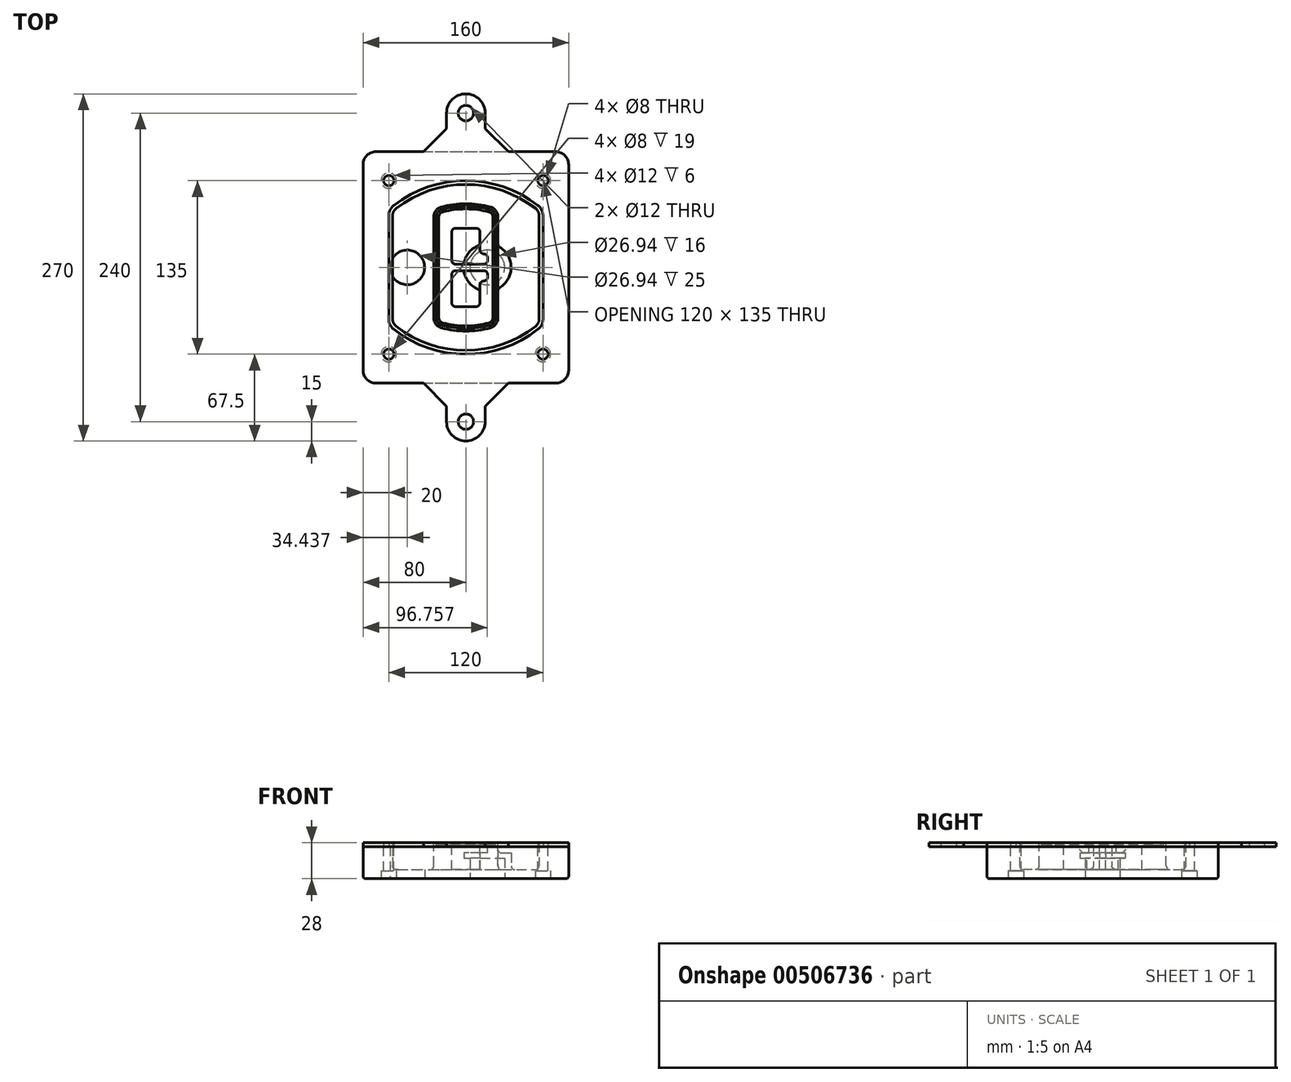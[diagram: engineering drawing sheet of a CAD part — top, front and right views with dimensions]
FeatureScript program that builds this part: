
annotation { "Feature Type Name" : "Feature", "Feature Type Description" : "" }
export const myFeature = defineFeature(function(context is Context, id is Id, definition is map)
    precondition{}
    {
        {
            var Q0;
            Q0=qCreatedBy(makeId("Top.planeOp"),FACE);
            var sketch = newSketch(context, id + "F0", { "sketchPlane" : qUnion([Q0])});
            skPoint(sketch, "E0.rect.middle", {"position": v(0, 0) * mm});
            skLineSegment(sketch, "E1.bottom", {"start": v(-70, -90) * mm, "end": v(70, -90) * mm});
            skLineSegment(sketch, "E1.top", {"start": v(-70, 90) * mm, "end": v(70, 90) * mm});
            skLineSegment(sketch, "E1.left", {"start": v(-80, -80) * mm, "end": v(-80, 80) * mm});
            skLineSegment(sketch, "E1.right", {"start": v(80, -80) * mm, "end": v(80, 80) * mm});
            skLineSegment(sketch, "E2", {"start": v(-80, 90) * mm, "end": v(80, -90) * mm, "construction": true});
            skLineSegment(sketch, "E3", {"start": v(80, 90) * mm, "end": v(-80, -90) * mm, "construction": true});
            skCircle(sketch, "E4", {"center": v(-60, 67.5) * mm, "radius": 4 * mm});
            skCircle(sketch, "E5", {"center": v(60, 67.5) * mm, "radius": 4 * mm});
            skCircle(sketch, "E6", {"center": v(60, -67.5) * mm, "radius": 4 * mm});
            skCircle(sketch, "E7", {"center": v(-60, -67.5) * mm, "radius": 4 * mm});
            skLineSegment(sketch, "E8", {"start": v(-60, 67.5) * mm, "end": v(60, 67.5) * mm, "construction": true});
            skLineSegment(sketch, "E9", {"start": v(60, 67.5) * mm, "end": v(60, -67.5) * mm, "construction": true});
            skLineSegment(sketch, "E10", {"start": v(60, -67.5) * mm, "end": v(-60, -67.5) * mm, "construction": true});
            skLineSegment(sketch, "E11", {"start": v(-60, -67.5) * mm, "end": v(-60, 67.5) * mm, "construction": true});
            skLineSegment(sketch, "E12", {"start": v(-60, 40.3) * mm, "end": v(-60, -40.3) * mm});
            skLineSegment(sketch, "E13", {"start": v(60, 40.3) * mm, "end": v(60, -40.3) * mm});
            skArc(sketch, "E14", {"start": v(56.15, 48.18) * mm, "mid": v(0, 67.5) * mm, "end": v(-56.15, 48.18) * mm});
            skArc(sketch, "E15", {"start": v(-56.15, -48.18) * mm, "mid": v(0, -67.5) * mm, "end": v(56.15, -48.18) * mm});
            skLineSegment(sketch, "E16", {"start": v(-60, 0) * mm, "end": v(60, 0) * mm, "construction": true});
            skPoint(sketch, "E17.visualSharp", {"position": v(-60, -45) * mm});
            skArc(sketch, "E17.filletArc", {"start": v(-60, -40.3) * mm, "mid": v(-58.99, -44.68) * mm, "end": v(-56.15, -48.18) * mm});
            skPoint(sketch, "E18.visualSharp", {"position": v(-60, 45) * mm});
            skArc(sketch, "E18.filletArc", {"start": v(-56.15, 48.18) * mm, "mid": v(-58.99, 44.68) * mm, "end": v(-60, 40.3) * mm});
            skPoint(sketch, "E19.visualSharp", {"position": v(60, 45) * mm});
            skArc(sketch, "E19.filletArc", {"start": v(60, 40.3) * mm, "mid": v(58.99, 44.68) * mm, "end": v(56.15, 48.18) * mm});
            skPoint(sketch, "E20.visualSharp", {"position": v(60, -45) * mm});
            skArc(sketch, "E20.filletArc", {"start": v(56.15, -48.18) * mm, "mid": v(58.99, -44.68) * mm, "end": v(60, -40.3) * mm});
            skPoint(sketch, "E21.visualSharp", {"position": v(-80, 90) * mm});
            skArc(sketch, "E21.filletArc", {"start": v(-70, 90) * mm, "mid": v(-77.07, 87.07) * mm, "end": v(-80, 80) * mm});
            skPoint(sketch, "E22.visualSharp", {"position": v(80, 90) * mm});
            skArc(sketch, "E22.filletArc", {"start": v(80, 80) * mm, "mid": v(77.07, 87.07) * mm, "end": v(70, 90) * mm});
            skPoint(sketch, "E23.visualSharp", {"position": v(80, -90) * mm});
            skArc(sketch, "E23.filletArc", {"start": v(70, -90) * mm, "mid": v(77.07, -87.07) * mm, "end": v(80, -80) * mm});
            skPoint(sketch, "E24.visualSharp", {"position": v(-80, -90) * mm});
            skArc(sketch, "E24.filletArc", {"start": v(-80, -80) * mm, "mid": v(-77.07, -87.07) * mm, "end": v(-70, -90) * mm});
            skArc(sketch, "E25.0", {"start": v(57, 40.3) * mm, "mid": v(56.3, 43.36) * mm, "end": v(54.3, 45.81) * mm});
            skLineSegment(sketch, "E25.1", {"start": v(57, 40.3) * mm, "end": v(57, -40.3) * mm});
            skArc(sketch, "E25.2", {"start": v(54.3, -45.81) * mm, "mid": v(56.3, -43.36) * mm, "end": v(57, -40.3) * mm});
            skArc(sketch, "E25.3", {"start": v(-54.3, -45.81) * mm, "mid": v(0, -64.5) * mm, "end": v(54.3, -45.81) * mm});
            skArc(sketch, "E25.4", {"start": v(-57, -40.3) * mm, "mid": v(-56.3, -43.36) * mm, "end": v(-54.3, -45.81) * mm});
            skArc(sketch, "E25.5", {"start": v(54.3, 45.81) * mm, "mid": v(0, 64.5) * mm, "end": v(-54.3, 45.81) * mm});
            skLineSegment(sketch, "E25.6", {"start": v(-57, 40.3) * mm, "end": v(-57, -40.3) * mm});
            skArc(sketch, "E25.7", {"start": v(-54.3, 45.81) * mm, "mid": v(-56.3, 43.36) * mm, "end": v(-57, 40.3) * mm});
            skArc(sketch, "E26.0", {"start": v(-58.62, 51.33) * mm, "mid": v(-62.58, 46.43) * mm, "end": v(-64, 40.3) * mm});
            skArc(sketch, "E26.1", {"start": v(58.62, 51.33) * mm, "mid": v(0, 71.5) * mm, "end": v(-58.62, 51.33) * mm});
            skArc(sketch, "E26.2", {"start": v(64, 40.3) * mm, "mid": v(62.58, 46.43) * mm, "end": v(58.62, 51.33) * mm});
            skLineSegment(sketch, "E26.3", {"start": v(64, 40.3) * mm, "end": v(64, -40.3) * mm});
            skArc(sketch, "E26.4", {"start": v(58.62, -51.33) * mm, "mid": v(62.58, -46.43) * mm, "end": v(64, -40.3) * mm});
            skLineSegment(sketch, "E26.5", {"start": v(-64, 40.3) * mm, "end": v(-64, -40.3) * mm});
            skArc(sketch, "E26.6", {"start": v(-58.62, -51.33) * mm, "mid": v(0, -71.5) * mm, "end": v(58.62, -51.33) * mm});
            skArc(sketch, "E26.7", {"start": v(-64, -40.3) * mm, "mid": v(-62.58, -46.43) * mm, "end": v(-58.62, -51.33) * mm});
            skSolve(sketch);
        }
        {
            var Q0;
            Q0=makeQuery(id+"F0.imprint","IMPRINT",FACE,{"disambiguationData":[TD([[makeQuery(id+"F0.imprint","IMPRINT",EDGE,{"derivedFrom":sQuery(id+"F0.wireOp",EDGE,"E1.bottom")}),1.0]])]});
            var Q1;
            Q1=makeQuery(id+"F0.imprint","IMPRINT",FACE,{"disambiguationData":[TD([[makeQuery(id+"F0.imprint","IMPRINT",EDGE,{"derivedFrom":sQuery(id+"F0.wireOp",EDGE,"E12")}),1.0]])]});
            var Q2;
            Q2=makeQuery(id+"F0.imprint","IMPRINT",FACE,{"disambiguationData":[TD([[makeQuery(id+"F0.imprint","IMPRINT",EDGE,{"derivedFrom":sQuery(id+"F0.wireOp",EDGE,"E25.0")}),1.0]])]});
            var Q3;
            Q3=makeQuery(id+"F0.imprint","IMPRINT",FACE,{"disambiguationData":[TD([[makeQuery(id+"F0.imprint","IMPRINT",EDGE,{"derivedFrom":sQuery(id+"F0.wireOp",EDGE,"E12")}),-1.0]])]});
            extrude(context, id + "F1", {"entities" : qUnion([Q0, Q1, Q2, Q3]), "oppositeDirection" : true, "depth" : 25 * mm});
        }
        {
            var Q0;
            Q0=makeQuery(id+"F0.imprint","IMPRINT",FACE,{"disambiguationData":[TD([[makeQuery(id+"F0.imprint","IMPRINT",EDGE,{"derivedFrom":sQuery(id+"F0.wireOp",EDGE,"E12")}),1.0]])]});
            extrude(context, id + "F2", {"entities" : qUnion([Q0]), "operationType" : NewBodyOperationType.ADD, "depth" : 3 * mm});
        }
        {
            var Q0;
            Q0=makeQuery(id+"F0.imprint","IMPRINT",FACE,{"disambiguationData":[TD([[makeQuery(id+"F0.imprint","IMPRINT",EDGE,{"derivedFrom":sQuery(id+"F0.wireOp",EDGE,"E25.0")}),1.0]])]});
            extrude(context, id + "F3", {"entities" : qUnion([Q0]), "operationType" : NewBodyOperationType.REMOVE, "oppositeDirection" : true, "depth" : 18 * mm});
        }
        {
            var Q0;
            Q0=makeQuery(id+"F2.opExtrude","CAP_FACE",FACE,{"disambiguationData":[OSD([sQuery(id+"F0.wireOp",EDGE,"E12"),sQuery(id+"F0.wireOp",EDGE,"E13"),sQuery(id+"F0.wireOp",EDGE,"E14"),sQuery(id+"F0.wireOp",EDGE,"E15"),sQuery(id+"F0.wireOp",EDGE,"E17.filletArc"),sQuery(id+"F0.wireOp",EDGE,"E18.filletArc"),sQuery(id+"F0.wireOp",EDGE,"E19.filletArc"),sQuery(id+"F0.wireOp",EDGE,"E20.filletArc"),sQuery(id+"F0.wireOp",EDGE,"E25.0"),sQuery(id+"F0.wireOp",EDGE,"E25.1"),sQuery(id+"F0.wireOp",EDGE,"E25.2"),sQuery(id+"F0.wireOp",EDGE,"E25.3"),sQuery(id+"F0.wireOp",EDGE,"E25.4"),sQuery(id+"F0.wireOp",EDGE,"E25.5"),sQuery(id+"F0.wireOp",EDGE,"E25.6"),sQuery(id+"F0.wireOp",EDGE,"E25.7")])],"isStart":false});
            var sketch = newSketch(context, id + "F4", { "sketchPlane" : qUnion([Q0])});
            skArc(sketch, "E27.0", {"start": v(-19.08, -46.97) * mm, "mid": v(0, -49.5) * mm, "end": v(19.08, -46.97) * mm});
            skArc(sketch, "E28.0", {"start": v(19.08, 46.97) * mm, "mid": v(0, 49.5) * mm, "end": v(-19.08, 46.97) * mm});
            skLineSegment(sketch, "E29", {"start": v(-25, 39.25) * mm, "end": v(-25, -39.25) * mm});
            skLineSegment(sketch, "E30", {"start": v(25, 39.25) * mm, "end": v(25, -39.25) * mm});
            skLineSegment(sketch, "E31", {"start": v(-25, 45.1) * mm, "end": v(25, 45.1) * mm, "construction": true});
            skLineSegment(sketch, "E32", {"start": v(-25, -45.1) * mm, "end": v(25, -45.1) * mm, "construction": true});
            skPoint(sketch, "E33.visualSharp", {"position": v(-25, 45.1) * mm});
            skArc(sketch, "E33.filletArc", {"start": v(-19.08, 46.97) * mm, "mid": v(-23.35, 44.11) * mm, "end": v(-25, 39.25) * mm});
            skPoint(sketch, "E34.visualSharp", {"position": v(25, 45.1) * mm});
            skArc(sketch, "E34.filletArc", {"start": v(25, 39.25) * mm, "mid": v(23.35, 44.11) * mm, "end": v(19.08, 46.97) * mm});
            skPoint(sketch, "E35.visualSharp", {"position": v(25, -45.1) * mm});
            skArc(sketch, "E35.filletArc", {"start": v(19.08, -46.97) * mm, "mid": v(23.35, -44.11) * mm, "end": v(25, -39.25) * mm});
            skPoint(sketch, "E36.visualSharp", {"position": v(-25, -45.1) * mm});
            skArc(sketch, "E36.filletArc", {"start": v(-25, -39.25) * mm, "mid": v(-23.35, -44.11) * mm, "end": v(-19.08, -46.97) * mm});
            skArc(sketch, "E37.0", {"start": v(54.3, 45.81) * mm, "mid": v(0, 64.5) * mm, "end": v(-54.3, 45.81) * mm});
            skArc(sketch, "E37.1", {"start": v(-54.3, 45.81) * mm, "mid": v(-56.3, 43.36) * mm, "end": v(-57, 40.3) * mm});
            skLineSegment(sketch, "E37.2", {"start": v(-57, 40.3) * mm, "end": v(-57, -40.3) * mm});
            skArc(sketch, "E37.3", {"start": v(-57, -40.3) * mm, "mid": v(-56.3, -43.36) * mm, "end": v(-54.3, -45.81) * mm});
            skArc(sketch, "E37.4", {"start": v(-54.3, -45.81) * mm, "mid": v(0, -64.5) * mm, "end": v(54.3, -45.81) * mm});
            skArc(sketch, "E37.5", {"start": v(54.3, -45.81) * mm, "mid": v(56.3, -43.36) * mm, "end": v(57, -40.3) * mm});
            skLineSegment(sketch, "E37.6", {"start": v(57, 40.3) * mm, "end": v(57, -40.3) * mm});
            skArc(sketch, "E37.7", {"start": v(57, 40.3) * mm, "mid": v(56.3, 43.36) * mm, "end": v(54.3, 45.81) * mm});
            skLineSegment(sketch, "E38.0", {"start": v(23, 39.25) * mm, "end": v(23, -39.25) * mm});
            skArc(sketch, "E38.1", {"start": v(18.56, -45.04) * mm, "mid": v(21.76, -42.9) * mm, "end": v(23, -39.25) * mm});
            skArc(sketch, "E38.2", {"start": v(-18.56, -45.04) * mm, "mid": v(0, -47.5) * mm, "end": v(18.56, -45.04) * mm});
            skArc(sketch, "E38.3", {"start": v(-23, -39.25) * mm, "mid": v(-21.76, -42.9) * mm, "end": v(-18.56, -45.04) * mm});
            skLineSegment(sketch, "E38.4", {"start": v(-23, 39.25) * mm, "end": v(-23, -39.25) * mm});
            skArc(sketch, "E38.5", {"start": v(23, 39.25) * mm, "mid": v(21.76, 42.9) * mm, "end": v(18.56, 45.04) * mm});
            skArc(sketch, "E38.6", {"start": v(-18.56, 45.04) * mm, "mid": v(-21.76, 42.9) * mm, "end": v(-23, 39.25) * mm});
            skArc(sketch, "E38.7", {"start": v(18.56, 45.04) * mm, "mid": v(0, 47.5) * mm, "end": v(-18.56, 45.04) * mm});
            skArc(sketch, "E39.0", {"start": v(21, 39.25) * mm, "mid": v(20.18, 41.68) * mm, "end": v(18.04, 43.1) * mm});
            skLineSegment(sketch, "E39.1", {"start": v(21, 39.25) * mm, "end": v(21, -39.25) * mm});
            skArc(sketch, "E39.2", {"start": v(18.04, -43.1) * mm, "mid": v(20.18, -41.68) * mm, "end": v(21, -39.25) * mm});
            skArc(sketch, "E39.3", {"start": v(-18.04, -43.1) * mm, "mid": v(0, -45.5) * mm, "end": v(18.04, -43.1) * mm});
            skArc(sketch, "E39.4", {"start": v(-21, -39.25) * mm, "mid": v(-20.18, -41.68) * mm, "end": v(-18.04, -43.1) * mm});
            skArc(sketch, "E39.5", {"start": v(18.04, 43.1) * mm, "mid": v(0, 45.5) * mm, "end": v(-18.04, 43.1) * mm});
            skLineSegment(sketch, "E39.6", {"start": v(-21, 39.25) * mm, "end": v(-21, -39.25) * mm});
            skArc(sketch, "E39.7", {"start": v(-18.04, 43.1) * mm, "mid": v(-20.18, 41.68) * mm, "end": v(-21, 39.25) * mm});
            skLineSegment(sketch, "E40", {"start": v(-25, 0) * mm, "end": v(25, 0) * mm, "construction": true});
            skLineSegment(sketch, "E41", {"start": v(-11, 5.5) * mm, "end": v(-11, 27.5) * mm});
            skLineSegment(sketch, "E42", {"start": v(-8, 30.5) * mm, "end": v(8, 30.5) * mm});
            skLineSegment(sketch, "E43", {"start": v(11, 27.5) * mm, "end": v(11, 13.5) * mm});
            skLineSegment(sketch, "E44", {"start": v(14, 10.5) * mm, "end": v(14, 10.5) * mm});
            skLineSegment(sketch, "E45", {"start": v(17, 7.5) * mm, "end": v(17, 5.5) * mm});
            skLineSegment(sketch, "E46", {"start": v(14, 2.5) * mm, "end": v(-8, 2.5) * mm});
            skPoint(sketch, "E47.visualSharp", {"position": v(-11, 30.5) * mm});
            skArc(sketch, "E47.filletArc", {"start": v(-8, 30.5) * mm, "mid": v(-10.12, 29.62) * mm, "end": v(-11, 27.5) * mm});
            skPoint(sketch, "E48.visualSharp", {"position": v(11, 30.5) * mm});
            skArc(sketch, "E48.filletArc", {"start": v(11, 27.5) * mm, "mid": v(10.12, 29.62) * mm, "end": v(8, 30.5) * mm});
            skPoint(sketch, "E49.visualSharp", {"position": v(11, 10.5) * mm});
            skArc(sketch, "E49.filletArc", {"start": v(11, 13.5) * mm, "mid": v(11.88, 11.38) * mm, "end": v(14, 10.5) * mm});
            skPoint(sketch, "E50.visualSharp", {"position": v(17, 10.5) * mm});
            skArc(sketch, "E50.filletArc", {"start": v(17, 7.5) * mm, "mid": v(16.12, 9.62) * mm, "end": v(14, 10.5) * mm});
            skPoint(sketch, "E51.visualSharp", {"position": v(17, 2.5) * mm});
            skArc(sketch, "E51.filletArc", {"start": v(14, 2.5) * mm, "mid": v(16.12, 3.38) * mm, "end": v(17, 5.5) * mm});
            skPoint(sketch, "E52.visualSharp", {"position": v(-11, 2.5) * mm});
            skArc(sketch, "E52.filletArc", {"start": v(-11, 5.5) * mm, "mid": v(-10.12, 3.38) * mm, "end": v(-8, 2.5) * mm});
            skLineSegment(sketch, "E53.0.MirrorCS", {"start": v(14, -2.5) * mm, "end": v(-8, -2.5) * mm});
            skArc(sketch, "E54.0.MirrorCS", {"start": v(-11, -5.5) * mm, "mid": v(-10.12, -3.38) * mm, "end": v(-8, -2.5) * mm});
            skLineSegment(sketch, "E55.0.MirrorCS", {"start": v(-11, -5.5) * mm, "end": v(-11, -27.5) * mm});
            skArc(sketch, "E56.0.MirrorCS", {"start": v(-8, -30.5) * mm, "mid": v(-10.12, -29.62) * mm, "end": v(-11, -27.5) * mm});
            skLineSegment(sketch, "E57.0.MirrorCS", {"start": v(-8, -30.5) * mm, "end": v(8, -30.5) * mm});
            skArc(sketch, "E58.0.MirrorCS", {"start": v(11, -27.5) * mm, "mid": v(10.12, -29.62) * mm, "end": v(8, -30.5) * mm});
            skLineSegment(sketch, "E59.0.MirrorCS", {"start": v(11, -27.5) * mm, "end": v(11, -13.5) * mm});
            skArc(sketch, "E60.0.MirrorCS", {"start": v(11, -13.5) * mm, "mid": v(11.88, -11.38) * mm, "end": v(14, -10.5) * mm});
            skArc(sketch, "E61.0.MirrorCS", {"start": v(17, -7.5) * mm, "mid": v(16.12, -9.62) * mm, "end": v(14, -10.5) * mm});
            skLineSegment(sketch, "E62.0.MirrorCS", {"start": v(17, -7.5) * mm, "end": v(17, -5.5) * mm});
            skArc(sketch, "E63.0.MirrorCS", {"start": v(14, -2.5) * mm, "mid": v(16.12, -3.38) * mm, "end": v(17, -5.5) * mm});
            skSolve(sketch);
        }
        {
            var Q0;
            Q0=makeQuery(id+"F4.imprint","IMPRINT",FACE,{"disambiguationData":[TD([[makeQuery(id+"F4.imprint","IMPRINT",EDGE,{"derivedFrom":sQuery(id+"F4.wireOp",EDGE,"E27.0")}),1.0]])]});
            var Q1;
            Q1=makeQuery(id+"F4.imprint","IMPRINT",FACE,{"disambiguationData":[TD([[makeQuery(id+"F4.imprint","IMPRINT",EDGE,{"derivedFrom":sQuery(id+"F4.wireOp",EDGE,"E38.0")}),-1.0]])]});
            var Q2;
            Q2=makeQuery(id+"F4.imprint","IMPRINT",FACE,{"disambiguationData":[TD([[makeQuery(id+"F4.imprint","IMPRINT",EDGE,{"derivedFrom":sQuery(id+"F4.wireOp",EDGE,"E39.0")}),1.0]])]});
            extrude(context, id + "F5", {"entities" : qUnion([Q0, Q1, Q2]), "operationType" : NewBodyOperationType.ADD, "endBound" : BoundingType.UP_TO_NEXT, "oppositeDirection" : true, "depth" : 25 * mm});
        }
        {
            var Q0;
            Q0=makeQuery(id+"F4.imprint","IMPRINT",FACE,{"disambiguationData":[TD([[makeQuery(id+"F4.imprint","IMPRINT",EDGE,{"derivedFrom":sQuery(id+"F4.wireOp",EDGE,"E38.0")}),-1.0]])]});
            extrude(context, id + "F6", {"entities" : qUnion([Q0]), "operationType" : NewBodyOperationType.REMOVE, "oppositeDirection" : true, "depth" : 2 * mm});
        }
        {
            var Q0;
            Q0=makeQuery(id+"F1.opExtrude","CAP_FACE",FACE,{"disambiguationData":[OSD([sQuery(id+"F0.wireOp",EDGE,"E1.bottom"),sQuery(id+"F0.wireOp",EDGE,"E1.top"),sQuery(id+"F0.wireOp",EDGE,"E1.left"),sQuery(id+"F0.wireOp",EDGE,"E1.right"),sQuery(id+"F0.wireOp",EDGE,"E4"),sQuery(id+"F0.wireOp",EDGE,"E5"),sQuery(id+"F0.wireOp",EDGE,"E6"),sQuery(id+"F0.wireOp",EDGE,"E7"),sQuery(id+"F0.wireOp",EDGE,"E21.filletArc"),sQuery(id+"F0.wireOp",EDGE,"E22.filletArc"),sQuery(id+"F0.wireOp",EDGE,"E23.filletArc"),sQuery(id+"F0.wireOp",EDGE,"E24.filletArc")])],"isStart":false});
            var sketch = newSketch(context, id + "F7", { "sketchPlane" : qUnion([Q0])});
            skCircle(sketch, "E64", {"center": v(16.76, 0) * mm, "radius": 13.47 * mm});
            skCircle(sketch, "E65", {"center": v(-45.56, 0) * mm, "radius": 13.47 * mm});
            skLineSegment(sketch, "E66", {"start": v(80, 0) * mm, "end": v(-80, 0) * mm});
            skCircle(sketch, "E67", {"center": v(16.76, 0) * mm, "radius": 18.47 * mm});
            skCircle(sketch, "E68", {"center": v(60, -67.5) * mm, "radius": 6 * mm});
            skCircle(sketch, "E69", {"center": v(-60, -67.5) * mm, "radius": 6 * mm});
            skCircle(sketch, "E70", {"center": v(-60, 67.5) * mm, "radius": 6 * mm});
            skCircle(sketch, "E71", {"center": v(60, 67.5) * mm, "radius": 6 * mm});
            skSolve(sketch);
        }
        {
            var Q0;
            {var subQ1=sQuery(id+"F7.wireOp",EDGE,"E66");var subQ4=sQuery(id+"F7.wireOp",EDGE,"E64");var subQ6=makeQuery(id+"F7.imprint","INTERSECT",VERTEX,{"disambiguationData":[OD(0.0)],"derivedFrom":[subQ4,subQ1]});Q0=makeQuery(id+"F7.imprint","IMPRINT",FACE,{"disambiguationData":[TD([[makeQuery(id+"F7.imprint","IMPRINT",EDGE,{"disambiguationData":[TD([[subQ6,-1.0]])],"derivedFrom":subQ4}),-1.0]])]});}
            var Q1;
            {var subQ0=sQuery(id+"F7.wireOp",EDGE,"E66");var subQ1=sQuery(id+"F7.wireOp",EDGE,"E64");var subQ3=makeQuery(id+"F7.imprint","INTERSECT",VERTEX,{"disambiguationData":[OD(0.0)],"derivedFrom":[subQ1,subQ0]});Q1=makeQuery(id+"F7.imprint","IMPRINT",FACE,{"disambiguationData":[TD([[makeQuery(id+"F7.imprint","IMPRINT",EDGE,{"disambiguationData":[TD([[subQ3,-1.0]])],"derivedFrom":subQ1}),1.0]])]});}
            var Q2;
            {var subQ0=sQuery(id+"F7.wireOp",EDGE,"E66");var subQ1=sQuery(id+"F7.wireOp",EDGE,"E64");var subQ3=makeQuery(id+"F7.imprint","INTERSECT",VERTEX,{"disambiguationData":[OD(0.0)],"derivedFrom":[subQ1,subQ0]});Q2=makeQuery(id+"F7.imprint","IMPRINT",FACE,{"disambiguationData":[TD([[makeQuery(id+"F7.imprint","IMPRINT",EDGE,{"disambiguationData":[TD([[subQ3,1.0]])],"derivedFrom":subQ1}),1.0]])]});}
            var Q3;
            {var subQ1=sQuery(id+"F7.wireOp",EDGE,"E66");var subQ4=sQuery(id+"F7.wireOp",EDGE,"E64");var subQ6=makeQuery(id+"F7.imprint","INTERSECT",VERTEX,{"disambiguationData":[OD(0.0)],"derivedFrom":[subQ4,subQ1]});Q3=makeQuery(id+"F7.imprint","IMPRINT",FACE,{"disambiguationData":[TD([[makeQuery(id+"F7.imprint","IMPRINT",EDGE,{"disambiguationData":[TD([[subQ6,1.0]])],"derivedFrom":subQ4}),-1.0]])]});}
            extrude(context, id + "F8", {"entities" : qUnion([Q0, Q1, Q2, Q3]), "operationType" : NewBodyOperationType.ADD, "oppositeDirection" : true, "depth" : 20 * mm});
        }
        {
            var Q0;
            {var subQ0=sQuery(id+"F7.wireOp",EDGE,"E66");var subQ1=sQuery(id+"F7.wireOp",EDGE,"E64");var subQ3=makeQuery(id+"F7.imprint","INTERSECT",VERTEX,{"disambiguationData":[OD(0.0)],"derivedFrom":[subQ1,subQ0]});Q0=makeQuery(id+"F7.imprint","IMPRINT",FACE,{"disambiguationData":[TD([[makeQuery(id+"F7.imprint","IMPRINT",EDGE,{"disambiguationData":[TD([[subQ3,-1.0]])],"derivedFrom":subQ1}),1.0]])]});}
            var Q1;
            {var subQ0=sQuery(id+"F7.wireOp",EDGE,"E66");var subQ1=sQuery(id+"F7.wireOp",EDGE,"E64");var subQ3=makeQuery(id+"F7.imprint","INTERSECT",VERTEX,{"disambiguationData":[OD(0.0)],"derivedFrom":[subQ1,subQ0]});Q1=makeQuery(id+"F7.imprint","IMPRINT",FACE,{"disambiguationData":[TD([[makeQuery(id+"F7.imprint","IMPRINT",EDGE,{"disambiguationData":[TD([[subQ3,1.0]])],"derivedFrom":subQ1}),1.0]])]});}
            extrude(context, id + "F9", {"entities" : qUnion([Q0, Q1]), "operationType" : NewBodyOperationType.REMOVE, "oppositeDirection" : true, "depth" : 16 * mm});
        }
        {
            var Q0;
            {var subQ0=sQuery(id+"F7.wireOp",EDGE,"E66");var subQ1=sQuery(id+"F7.wireOp",EDGE,"E65");var subQ3=makeQuery(id+"F7.imprint","INTERSECT",VERTEX,{"disambiguationData":[OD(0.0)],"derivedFrom":[subQ1,subQ0]});Q0=makeQuery(id+"F7.imprint","IMPRINT",FACE,{"disambiguationData":[TD([[makeQuery(id+"F7.imprint","IMPRINT",EDGE,{"disambiguationData":[TD([[subQ3,-1.0]])],"derivedFrom":subQ1}),1.0]])]});}
            var Q1;
            {var subQ0=sQuery(id+"F7.wireOp",EDGE,"E66");var subQ1=sQuery(id+"F7.wireOp",EDGE,"E65");var subQ3=makeQuery(id+"F7.imprint","INTERSECT",VERTEX,{"disambiguationData":[OD(0.0)],"derivedFrom":[subQ1,subQ0]});Q1=makeQuery(id+"F7.imprint","IMPRINT",FACE,{"disambiguationData":[TD([[makeQuery(id+"F7.imprint","IMPRINT",EDGE,{"disambiguationData":[TD([[subQ3,1.0]])],"derivedFrom":subQ1}),1.0]])]});}
            extrude(context, id + "F10", {"entities" : qUnion([Q0, Q1]), "operationType" : NewBodyOperationType.REMOVE, "oppositeDirection" : true, "depth" : 25 * mm});
        }
        {
            var Q0;
            Q0=makeQuery(id+"F7.imprint","IMPRINT",FACE,{"disambiguationData":[TD([[makeQuery(id+"F7.imprint","IMPRINT",EDGE,{"derivedFrom":sQuery(id+"F7.wireOp",EDGE,"E68")}),1.0]])]});
            var Q1;
            Q1=makeQuery(id+"F7.imprint","IMPRINT",FACE,{"disambiguationData":[TD([[makeQuery(id+"F7.imprint","IMPRINT",EDGE,{"derivedFrom":makeQuery(id+"F1.opExtrude","CAP_EDGE",EDGE,{"disambiguationData":[OSD([sQuery(id+"F0.wireOp",EDGE,"E5")])],"isStart":false})}),-1.0]])]});
            var Q2;
            Q2=makeQuery(id+"F7.imprint","IMPRINT",FACE,{"disambiguationData":[TD([[makeQuery(id+"F7.imprint","IMPRINT",EDGE,{"derivedFrom":sQuery(id+"F7.wireOp",EDGE,"E69")}),1.0]])]});
            var Q3;
            Q3=makeQuery(id+"F7.imprint","IMPRINT",FACE,{"disambiguationData":[TD([[makeQuery(id+"F7.imprint","IMPRINT",EDGE,{"derivedFrom":makeQuery(id+"F1.opExtrude","CAP_EDGE",EDGE,{"disambiguationData":[OSD([sQuery(id+"F0.wireOp",EDGE,"E4")])],"isStart":false})}),-1.0]])]});
            var Q4;
            Q4=makeQuery(id+"F7.imprint","IMPRINT",FACE,{"disambiguationData":[TD([[makeQuery(id+"F7.imprint","IMPRINT",EDGE,{"derivedFrom":sQuery(id+"F7.wireOp",EDGE,"E70")}),1.0]])]});
            var Q5;
            Q5=makeQuery(id+"F7.imprint","IMPRINT",FACE,{"disambiguationData":[TD([[makeQuery(id+"F7.imprint","IMPRINT",EDGE,{"derivedFrom":makeQuery(id+"F1.opExtrude","CAP_EDGE",EDGE,{"disambiguationData":[OSD([sQuery(id+"F0.wireOp",EDGE,"E7")])],"isStart":false})}),-1.0]])]});
            var Q6;
            Q6=makeQuery(id+"F7.imprint","IMPRINT",FACE,{"disambiguationData":[TD([[makeQuery(id+"F7.imprint","IMPRINT",EDGE,{"derivedFrom":sQuery(id+"F7.wireOp",EDGE,"E71")}),1.0]])]});
            var Q7;
            Q7=makeQuery(id+"F7.imprint","IMPRINT",FACE,{"disambiguationData":[TD([[makeQuery(id+"F7.imprint","IMPRINT",EDGE,{"derivedFrom":makeQuery(id+"F1.opExtrude","CAP_EDGE",EDGE,{"disambiguationData":[OSD([sQuery(id+"F0.wireOp",EDGE,"E6")])],"isStart":false})}),-1.0]])]});
            extrude(context, id + "F11", {"entities" : qUnion([Q0, Q1, Q2, Q3, Q4, Q5, Q6, Q7]), "operationType" : NewBodyOperationType.REMOVE, "oppositeDirection" : true, "depth" : 6 * mm});
        }
        {
            var Q0;
            Q0=makeQuery(id+"F9.boolean.opBoolean","COPY",FACE,{"derivedFrom":makeQuery(id+"F9.opExtrude","CAP_FACE",FACE,{"disambiguationData":[OSD([sQuery(id+"F7.wireOp",EDGE,"E64")])],"isStart":false})});
            var sketch = newSketch(context, id + "F12", { "sketchPlane" : qUnion([Q0])});
            skArc(sketch, "E72.0", {"start": v(11, 17.55) * mm, "mid": v(2.57, 11.82) * mm, "end": v(-1.54, 2.5) * mm});
            skArc(sketch, "E72.1", {"start": v(-1.54, -2.5) * mm, "mid": v(2.57, -11.82) * mm, "end": v(11, -17.55) * mm});
            skLineSegment(sketch, "E73", {"start": v(-1.54, -2.5) * mm, "end": v(14, -2.5) * mm});
            skLineSegment(sketch, "E74.0", {"start": v(14, 2.5) * mm, "end": v(-1.54, 2.5) * mm});
            skArc(sketch, "E74.1", {"start": v(14, 2.5) * mm, "mid": v(16.12, 3.38) * mm, "end": v(17, 5.5) * mm});
            skLineSegment(sketch, "E74.2", {"start": v(17, 7.5) * mm, "end": v(17, 5.5) * mm});
            skArc(sketch, "E74.3", {"start": v(17, 7.5) * mm, "mid": v(16.12, 9.62) * mm, "end": v(14, 10.5) * mm});
            skArc(sketch, "E74.4", {"start": v(11, 13.5) * mm, "mid": v(11.88, 11.38) * mm, "end": v(14, 10.5) * mm});
            skLineSegment(sketch, "E74.5", {"start": v(11, 17.55) * mm, "end": v(11, 13.5) * mm});
            skLineSegment(sketch, "E74.7", {"start": v(14, -2.5) * mm, "end": v(-1.54, -2.5) * mm});
            skArc(sketch, "E74.8", {"start": v(14, -2.5) * mm, "mid": v(16.12, -3.38) * mm, "end": v(17, -5.5) * mm});
            skLineSegment(sketch, "E74.9", {"start": v(17, -7.5) * mm, "end": v(17, -5.5) * mm});
            skArc(sketch, "E74.10", {"start": v(17, -7.5) * mm, "mid": v(16.12, -9.62) * mm, "end": v(14, -10.5) * mm});
            skArc(sketch, "E74.11", {"start": v(11, -13.5) * mm, "mid": v(11.88, -11.38) * mm, "end": v(14, -10.5) * mm});
            skLineSegment(sketch, "E74.12", {"start": v(11, -17.55) * mm, "end": v(11, -13.5) * mm});
            skPoint(sketch, "E75.orphan", {"position": v(11, -27.5) * mm});
            skPoint(sketch, "E76.orphan", {"position": v(-8, -2.5) * mm});
            skPoint(sketch, "E77.orphan", {"position": v(-8, 2.5) * mm});
            skPoint(sketch, "E78.orphan", {"position": v(11, 27.5) * mm});
            skSolve(sketch);
        }
        {
            var Q0;
            {var subQ7=sQuery(id+"F12.wireOp",EDGE,"E72.0");var subQ14=sQuery(id+"F12.wireOp",EDGE,"E72.1");var subQ16=sQuery(id+"F12.wireOp",EDGE,"E74.1");var subQ18=sQuery(id+"F12.wireOp",EDGE,"E74.8");Q0=qUnion([makeQuery(id+"F12.imprint","IMPRINT",FACE,{"disambiguationData":[TD([[makeQuery(id+"F12.imprint","IMPRINT",EDGE,{"derivedFrom":subQ7}),1.0]])]}),makeQuery(id+"F12.imprint","IMPRINT",FACE,{"disambiguationData":[TD([[makeQuery(id+"F12.imprint","IMPRINT",EDGE,{"derivedFrom":subQ14}),1.0]])]}),makeQuery(id+"F12.imprint","IMPRINT",FACE,{"disambiguationData":[TD([[makeQuery(id+"F12.imprint","IMPRINT",EDGE,{"derivedFrom":subQ16}),1.0]])]}),makeQuery(id+"F12.imprint","IMPRINT",FACE,{"disambiguationData":[TD([[makeQuery(id+"F12.imprint","IMPRINT",EDGE,{"derivedFrom":subQ18}),-1.0]])]})]);}
            var Q1;
            Q1=makeQuery(id+"F5.boolean.opBoolean","SPLIT",FACE,{"disambiguationData":[TD([makeQuery(id+"F5.opExtrude","SWEPT_FACE",FACE,{"disambiguationData":[OSD([sQuery(id+"F4.wireOp",EDGE,"E41")])]})])],"derivedFrom":makeQuery(id+"F3.boolean.opBoolean","COPY",FACE,{"derivedFrom":makeQuery(id+"F3.opExtrude","CAP_FACE",FACE,{"disambiguationData":[OSD([sQuery(id+"F0.wireOp",EDGE,"E25.0"),sQuery(id+"F0.wireOp",EDGE,"E25.1"),sQuery(id+"F0.wireOp",EDGE,"E25.2"),sQuery(id+"F0.wireOp",EDGE,"E25.3"),sQuery(id+"F0.wireOp",EDGE,"E25.4"),sQuery(id+"F0.wireOp",EDGE,"E25.5"),sQuery(id+"F0.wireOp",EDGE,"E25.6"),sQuery(id+"F0.wireOp",EDGE,"E25.7")])],"isStart":false})})});
            extrude(context, id + "F13", {"entities" : qUnion([Q0]), "operationType" : NewBodyOperationType.REMOVE, "endBound" : BoundingType.UP_TO_SURFACE, "endBoundEntityFace" : qUnion([Q1]), "depth" : 25 * mm});
        }
        {
            var Q0;
            Q0=makeQuery(id+"F3.boolean.opBoolean","COPY",EDGE,{"derivedFrom":makeQuery(id+"F3.opExtrude","CAP_EDGE",EDGE,{"disambiguationData":[OSD([sQuery(id+"F0.wireOp",EDGE,"E25.6")])],"isStart":false})});
            var Q1;
            Q1=makeQuery(id+"F8.boolean.opBoolean","INTERSECT",EDGE,{"derivedFrom":[makeQuery(id+"F5.opExtrude","SWEPT_FACE",FACE,{"disambiguationData":[OSD([sQuery(id+"F4.wireOp",EDGE,"E30")])]}),makeQuery(id+"F8.opExtrude","CAP_FACE",FACE,{"disambiguationData":[OSD([sQuery(id+"F7.wireOp",EDGE,"E67")])],"isStart":false})]});
            var Q2;
            Q2=makeQuery(id+"F8.boolean.opBoolean","INTERSECT",EDGE,{"disambiguationData":[OD(1.0)],"derivedFrom":[makeQuery(id+"F5.opExtrude","SWEPT_FACE",FACE,{"disambiguationData":[OSD([sQuery(id+"F4.wireOp",EDGE,"E30")])]}),makeQuery(id+"F8.opExtrude","SWEPT_FACE",FACE,{"disambiguationData":[OSD([sQuery(id+"F7.wireOp",EDGE,"E67")])]})]});
            var Q3;
            {var subQ0=sQuery(id+"F4.wireOp",EDGE,"E30");Q3=makeQuery(id+"F8.boolean.opBoolean","SPLIT",EDGE,{"disambiguationData":[TD([makeQuery(id+"F5.opExtrude","SWEPT_FACE",FACE,{"disambiguationData":[OSD([sQuery(id+"F4.wireOp",EDGE,"E35.filletArc")])]})])],"derivedFrom":makeQuery(id+"F5.opExtrude","CAP_EDGE",EDGE,{"disambiguationData":[OSD([subQ0])],"isStart":false})});}
            var Q4;
            {var subQ0=sQuery(id+"F0.wireOp",EDGE,"E25.7");var subQ1=sQuery(id+"F0.wireOp",EDGE,"E25.1");var subQ2=sQuery(id+"F0.wireOp",EDGE,"E25.6");var subQ3=sQuery(id+"F0.wireOp",EDGE,"E25.5");var subQ4=sQuery(id+"F0.wireOp",EDGE,"E25.4");var subQ5=sQuery(id+"F0.wireOp",EDGE,"E25.0");var subQ6=sQuery(id+"F0.wireOp",EDGE,"E25.2");var subQ7=sQuery(id+"F0.wireOp",EDGE,"E25.3");Q4=makeQuery(id+"F8.boolean.opBoolean","INTERSECT",EDGE,{"derivedFrom":[makeQuery(id+"F5.boolean.opBoolean","SPLIT",FACE,{"disambiguationData":[TD([makeQuery(id+"F2.opExtrude","SWEPT_FACE",FACE,{"disambiguationData":[OSD([subQ5])]})])],"derivedFrom":makeQuery(id+"F3.boolean.opBoolean","COPY",FACE,{"derivedFrom":makeQuery(id+"F3.opExtrude","CAP_FACE",FACE,{"disambiguationData":[OSD([subQ5,subQ1,subQ6,subQ7,subQ4,subQ3,subQ2,subQ0])],"isStart":false})})}),makeQuery(id+"F8.opExtrude","SWEPT_FACE",FACE,{"disambiguationData":[OSD([sQuery(id+"F7.wireOp",EDGE,"E67")])]})]});}
            var Q5;
            Q5=makeQuery(id+"F8.boolean.opBoolean","INTERSECT",EDGE,{"disambiguationData":[OD(0.0)],"derivedFrom":[makeQuery(id+"F5.opExtrude","SWEPT_FACE",FACE,{"disambiguationData":[OSD([sQuery(id+"F4.wireOp",EDGE,"E30")])]}),makeQuery(id+"F8.opExtrude","SWEPT_FACE",FACE,{"disambiguationData":[OSD([sQuery(id+"F7.wireOp",EDGE,"E67")])]})]});
            fillet(context, id + "F14", {"entities" : qUnion([Q0, Q1, Q2, Q3, Q4, Q5]), "radius" : 3 * mm, "tangentPropagation" : true, "allowEdgeOverflow" : false});
        }
        {
            var Q0;
            Q0=makeQuery(id+"F1.opExtrude","CAP_EDGE",EDGE,{"disambiguationData":[OSD([sQuery(id+"F0.wireOp",EDGE,"E1.bottom")])],"isStart":false});
            fillet(context, id + "F15", {"entities" : qUnion([Q0]), "radius" : 2 * mm, "tangentPropagation" : true, "allowEdgeOverflow" : false});
        }
        {
            var Q0;
            {var subQ0=sQuery(id+"F0.wireOp",EDGE,"E21.filletArc");var subQ1=sQuery(id+"F0.wireOp",EDGE,"E7");var subQ2=sQuery(id+"F0.wireOp",EDGE,"E6");var subQ3=sQuery(id+"F0.wireOp",EDGE,"E5");var subQ4=sQuery(id+"F0.wireOp",EDGE,"E4");var subQ5=sQuery(id+"F0.wireOp",EDGE,"E22.filletArc");var subQ6=sQuery(id+"F0.wireOp",EDGE,"E1.bottom");var subQ7=sQuery(id+"F0.wireOp",EDGE,"E1.right");var subQ8=sQuery(id+"F0.wireOp",EDGE,"E1.top");var subQ9=sQuery(id+"F0.wireOp",EDGE,"E1.left");var subQ10=sQuery(id+"F0.wireOp",EDGE,"E23.filletArc");var subQ11=sQuery(id+"F0.wireOp",EDGE,"E24.filletArc");Q0=makeQuery(id+"F2.boolean.opBoolean","SPLIT",FACE,{"disambiguationData":[TD([makeQuery(id+"F1.opExtrude","SWEPT_FACE",FACE,{"disambiguationData":[OSD([subQ6])]})])],"derivedFrom":makeQuery(id+"F1.opExtrude","CAP_FACE",FACE,{"disambiguationData":[OSD([subQ6,subQ8,subQ9,subQ7,subQ4,subQ3,subQ2,subQ1,subQ0,subQ5,subQ10,subQ11])],"isStart":true})});}
            var sketch = newSketch(context, id + "F16", { "sketchPlane" : qUnion([Q0])});
            skLineSegment(sketch, "E79", {"start": v(0, 90) * mm, "end": v(0, 120) * mm, "construction": true});
            skLineSegment(sketch, "E80", {"start": v(-33, 90) * mm, "end": v(-15, 108) * mm});
            skLineSegment(sketch, "E81", {"start": v(-15, 108) * mm, "end": v(-15, 120) * mm});
            skLineSegment(sketch, "E82", {"start": v(33, 90) * mm, "end": v(15, 108) * mm});
            skLineSegment(sketch, "E83", {"start": v(15, 108) * mm, "end": v(15, 120) * mm});
            skCircle(sketch, "E84", {"center": v(0, 120) * mm, "radius": 6 * mm});
            skArc(sketch, "E85", {"start": v(15, 120) * mm, "mid": v(0, 135) * mm, "end": v(-15, 120) * mm});
            skLineSegment(sketch, "E86", {"start": v(-80, 0) * mm, "end": v(80, 0) * mm, "construction": true});
            skLineSegment(sketch, "E87.MirrorCS", {"start": v(15, -108) * mm, "end": v(15, -120) * mm});
            skCircle(sketch, "E88.MirrorC", {"center": v(0, -120) * mm, "radius": 6 * mm});
            skLineSegment(sketch, "E89.MirrorCS", {"start": v(-15, -108) * mm, "end": v(-15, -120) * mm});
            skLineSegment(sketch, "E90.MirrorCS", {"start": v(33, -90) * mm, "end": v(15, -108) * mm});
            skLineSegment(sketch, "E91.MirrorCS", {"start": v(-33, -90) * mm, "end": v(-15, -108) * mm});
            skArc(sketch, "E92.MirrorCS", {"start": v(15, -120) * mm, "mid": v(0, -135) * mm, "end": v(-15, -120) * mm});
            skLineSegment(sketch, "E93.MirrorCS", {"start": v(0, -90) * mm, "end": v(0, -120) * mm, "construction": true});
            skSolve(sketch);
        }
        {
            var Q0;
            Q0=makeQuery(id+"F16.imprint","IMPRINT",FACE,{"disambiguationData":[TD([[makeQuery(id+"F16.imprint","IMPRINT",EDGE,{"derivedFrom":sQuery(id+"F16.wireOp",EDGE,"E87.MirrorCS")}),-1.0]])]});
            var Q1;
            Q1=makeQuery(id+"F16.imprint","IMPRINT",FACE,{"disambiguationData":[TD([[makeQuery(id+"F16.imprint","IMPRINT",EDGE,{"derivedFrom":makeQuery(id+"F1.opExtrude","CAP_EDGE",EDGE,{"disambiguationData":[OSD([sQuery(id+"F0.wireOp",EDGE,"E1.left")])],"isStart":true})}),-1.0]])]});
            var Q2;
            {var subQ1=sQuery(id+"F16.wireOp",EDGE,"E80");Q2=makeQuery(id+"F16.imprint","IMPRINT",FACE,{"disambiguationData":[TD([[makeQuery(id+"F16.imprint","IMPRINT",EDGE,{"derivedFrom":subQ1}),-1.0]])]});}
            var Q3;
            Q3=makeQuery(id+"F2.opExtrude","CAP_FACE",FACE,{"disambiguationData":[OSD([sQuery(id+"F0.wireOp",EDGE,"E12"),sQuery(id+"F0.wireOp",EDGE,"E13"),sQuery(id+"F0.wireOp",EDGE,"E14"),sQuery(id+"F0.wireOp",EDGE,"E15"),sQuery(id+"F0.wireOp",EDGE,"E17.filletArc"),sQuery(id+"F0.wireOp",EDGE,"E18.filletArc"),sQuery(id+"F0.wireOp",EDGE,"E19.filletArc"),sQuery(id+"F0.wireOp",EDGE,"E20.filletArc"),sQuery(id+"F0.wireOp",EDGE,"E25.0"),sQuery(id+"F0.wireOp",EDGE,"E25.1"),sQuery(id+"F0.wireOp",EDGE,"E25.2"),sQuery(id+"F0.wireOp",EDGE,"E25.3"),sQuery(id+"F0.wireOp",EDGE,"E25.4"),sQuery(id+"F0.wireOp",EDGE,"E25.5"),sQuery(id+"F0.wireOp",EDGE,"E25.6"),sQuery(id+"F0.wireOp",EDGE,"E25.7")])],"isStart":false});
            extrude(context, id + "F17", {"entities" : qUnion([Q0, Q1, Q2]), "endBound" : BoundingType.UP_TO_SURFACE, "endBoundEntityFace" : qUnion([Q3]), "depth" : 25 * mm});
        }
    });
